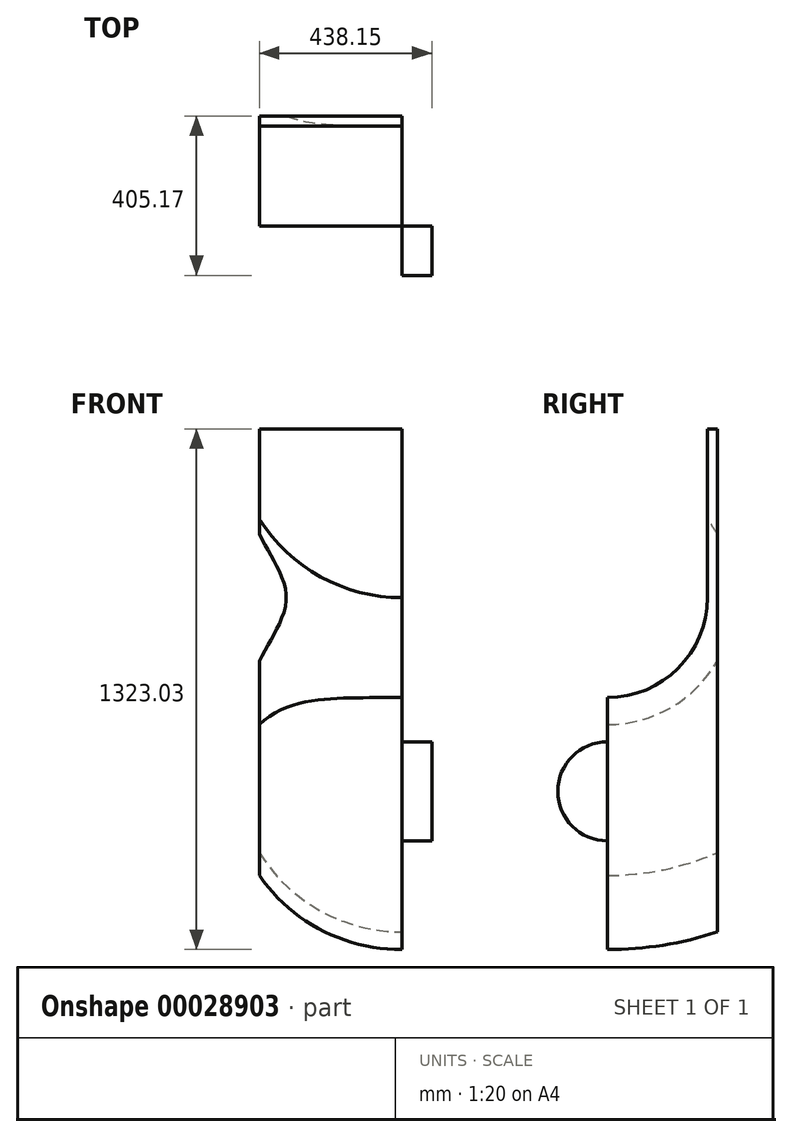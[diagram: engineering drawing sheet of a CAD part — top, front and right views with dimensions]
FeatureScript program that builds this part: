
annotation { "Feature Type Name" : "Feature", "Feature Type Description" : "" }
export const myFeature = defineFeature(function(context is Context, id is Id, definition is map)
    precondition{}
    {
        {
            var Q0;
            Q0=qCreatedBy(makeId("Front.planeOp"),FACE);
            var sketch = newSketch(context, id + "F0", { "sketchPlane" : qUnion([Q0])});
            skLineSegment(sketch, "E0", {"start": v(0, 0) * mm, "end": v(2438.4, 0) * mm});
            skLineSegment(sketch, "E1", {"start": v(2438.4, 0) * mm, "end": v(2438.4, 2438.4) * mm});
            skLineSegment(sketch, "E2", {"start": v(2438.4, 2438.4) * mm, "end": v(0, 2438.4) * mm});
            skLineSegment(sketch, "E3", {"start": v(0, 2438.4) * mm, "end": v(0, 0) * mm});
            skLineSegment(sketch, "E4", {"start": v(1219.2, 0) * mm, "end": v(1219.2, 457.2) * mm});
            skLineSegment(sketch, "E5", {"start": v(1219.2, 2438.4) * mm, "end": v(1882.77, 2438.4) * mm});
            skLineSegment(sketch, "E6", {"start": v(1219.2, 2438.4) * mm, "end": v(555.62, 2438.4) * mm});
            skLineSegment(sketch, "E7", {"start": v(555.62, 1981.2) * mm, "end": v(555.62, 1371.6) * mm});
            skLineSegment(sketch, "E8", {"start": v(1882.77, 1981.2) * mm, "end": v(1882.77, 1371.6) * mm});
            skLineSegment(sketch, "E9", {"start": v(1219.2, 0) * mm, "end": v(1219.2, 1352.55) * mm});
            skLineSegment(sketch, "E10", {"start": v(555.62, 1371.6) * mm, "end": v(1882.77, 1371.6) * mm});
            skLineSegment(sketch, "E11", {"start": v(1219.2, 1701.8) * mm, "end": v(1882.77, 1701.8) * mm});
            skLineSegment(sketch, "E12", {"start": v(2076.45, 457.2) * mm, "end": v(2076.45, 1981.2) * mm});
            skLineSegment(sketch, "E13", {"start": v(1219.2, 1701.8) * mm, "end": v(555.62, 1701.8) * mm});
            skLineSegment(sketch, "E14", {"start": v(361.95, 1981.2) * mm, "end": v(361.95, 457.2) * mm});
            skLineSegment(sketch, "E15", {"start": v(0, 0) * mm, "end": v(0, 457.2) * mm});
            skLineSegment(sketch, "E16", {"start": v(0, 457.2) * mm, "end": v(361.95, 457.2) * mm});
            skLineSegment(sketch, "E17", {"start": v(0, 2438.4) * mm, "end": v(0, 1981.2) * mm});
            skLineSegment(sketch, "E18", {"start": v(0, 1981.2) * mm, "end": v(361.95, 1981.2) * mm});
            skPoint(sketch, "E19.orphan", {"position": v(361.95, 0) * mm});
            skLineSegment(sketch, "E20.trimOffspring", {"start": v(555.62, 457.2) * mm, "end": v(1882.77, 457.2) * mm});
            skLineSegment(sketch, "E21.trimOffspring", {"start": v(2076.45, 457.2) * mm, "end": v(2438.4, 457.2) * mm});
            skPoint(sketch, "E22.orphan", {"position": v(2076.45, 0) * mm});
            skPoint(sketch, "E23.orphan", {"position": v(361.95, 2438.4) * mm});
            skPoint(sketch, "E24.orphan", {"position": v(361.95, 1701.8) * mm});
            skLineSegment(sketch, "E25.trimOffspring", {"start": v(555.62, 1981.2) * mm, "end": v(1882.77, 1981.2) * mm});
            skLineSegment(sketch, "E26.trimOffspring", {"start": v(2076.45, 1981.2) * mm, "end": v(2438.4, 1981.2) * mm});
            skPoint(sketch, "E27.orphan", {"position": v(2076.45, 1701.8) * mm});
            skLineSegment(sketch, "E28", {"start": v(555.62, 0) * mm, "end": v(549.28, 0) * mm});
            skLineSegment(sketch, "E29", {"start": v(549.28, 0) * mm, "end": v(549.28, 1352.55) * mm});
            skLineSegment(sketch, "E30", {"start": v(549.28, 0) * mm, "end": v(676.27, 0) * mm});
            skLineSegment(sketch, "E31", {"start": v(676.27, 0) * mm, "end": v(676.27, 1352.55) * mm});
            skLineSegment(sketch, "E32", {"start": v(1882.77, 0) * mm, "end": v(1889.13, 0) * mm});
            skLineSegment(sketch, "E33", {"start": v(1889.13, 0) * mm, "end": v(1762.13, 0) * mm});
            skLineSegment(sketch, "E34", {"start": v(1889.13, 0) * mm, "end": v(1889.13, 1352.55) * mm});
            skLineSegment(sketch, "E35", {"start": v(1762.13, 0) * mm, "end": v(1762.13, 1352.55) * mm});
            skLineSegment(sketch, "E36", {"start": v(412.75, 1371.6) * mm, "end": v(2025.65, 1371.6) * mm});
            skPoint(sketch, "E37.orphan", {"position": v(361.95, 1371.6) * mm});
            skLineSegment(sketch, "E38", {"start": v(412.75, 1371.6) * mm, "end": v(412.75, 1352.55) * mm});
            skLineSegment(sketch, "E39", {"start": v(412.75, 1352.55) * mm, "end": v(2025.65, 1352.55) * mm});
            skLineSegment(sketch, "E40", {"start": v(2025.65, 1352.55) * mm, "end": v(2025.65, 1371.6) * mm});
            skLineSegment(sketch, "E41.trimOffspring", {"start": v(1882.77, 1352.55) * mm, "end": v(1882.77, 0) * mm});
            skLineSegment(sketch, "E42.trimOffspring", {"start": v(1889.13, 1371.6) * mm, "end": v(1889.13, 2438.4) * mm});
            skLineSegment(sketch, "E43.trimOffspring", {"start": v(1762.13, 1371.6) * mm, "end": v(1762.13, 2438.4) * mm});
            skLineSegment(sketch, "E44.trimOffspring", {"start": v(1219.2, 1371.6) * mm, "end": v(1219.2, 1701.8) * mm});
            skLineSegment(sketch, "E45.trimOffspring", {"start": v(1219.2, 1371.6) * mm, "end": v(1219.2, 1981.2) * mm});
            skLineSegment(sketch, "E46.trimOffspring", {"start": v(549.28, 1371.6) * mm, "end": v(549.28, 2438.4) * mm});
            skLineSegment(sketch, "E47.trimOffspring", {"start": v(555.62, 1352.55) * mm, "end": v(555.62, 0) * mm});
            skLineSegment(sketch, "E48.trimOffspring", {"start": v(676.27, 1371.6) * mm, "end": v(676.27, 2438.4) * mm});
            skSolve(sketch);
        }
        {
            var Q0;
            Q0=makeQuery(id+"F0.imprint","IMPRINT",FACE,{"disambiguationData":[TD([[makeQuery(id+"F0.imprint","IMPRINT",EDGE,{"derivedFrom":sQuery(id+"F0.wireOp",EDGE,"E12")}),-1.0]])]});
            extrude(context, id + "F1", {"entities" : qUnion([Q0]), "depth" : 25.4 * mm});
        }
        {
            var Q0;
            Q0=makeQuery(id+"F1.opExtrude","CAP_FACE",FACE,{"disambiguationData":[OSD([sQuery(id+"F0.wireOp",EDGE,"E1"),sQuery(id+"F0.wireOp",EDGE,"E12"),sQuery(id+"F0.wireOp",EDGE,"E21.trimOffspring"),sQuery(id+"F0.wireOp",EDGE,"E26.trimOffspring")])],"isStart":false});
            var sketch = newSketch(context, id + "F2", { "sketchPlane" : qUnion([Q0])});
            skLineSegment(sketch, "E49.bottom", {"start": v(2076.45, 1552.47) * mm, "end": v(2438.4, 1552.47) * mm});
            skLineSegment(sketch, "E49.top", {"start": v(2076.45, 457.2) * mm, "end": v(2438.4, 457.2) * mm});
            skLineSegment(sketch, "E49.left", {"start": v(2076.45, 1552.47) * mm, "end": v(2076.45, 457.2) * mm});
            skLineSegment(sketch, "E49.right", {"start": v(2438.4, 1552.47) * mm, "end": v(2438.4, 457.2) * mm});
            skSolve(sketch);
        }
        {
            var Q0;
            Q0=makeQuery(id+"F2.imprint","IMPRINT",FACE,{"disambiguationData":[TD([[makeQuery(id+"F2.imprint","IMPRINT",EDGE,{"derivedFrom":sQuery(id+"F2.wireOp",EDGE,"E49.bottom")}),-1.0]])]});
            extrude(context, id + "F3", {"entities" : qUnion([Q0]), "operationType" : NewBodyOperationType.ADD, "depth" : 254 * mm});
        }
        {
            var Q0;
            Q0=makeQuery(id+"F1.opExtrude","CAP_FACE",FACE,{"disambiguationData":[OSD([sQuery(id+"F0.wireOp",EDGE,"E1"),sQuery(id+"F0.wireOp",EDGE,"E12"),sQuery(id+"F0.wireOp",EDGE,"E21.trimOffspring"),sQuery(id+"F0.wireOp",EDGE,"E26.trimOffspring")])],"isStart":false});
            var sketch = newSketch(context, id + "F4", { "sketchPlane" : qUnion([Q0])});
            skCircle(sketch, "E50", {"center": v(2438.4, 1981.2) * mm, "radius": 428.73 * mm});
            skSolve(sketch);
        }
        {
            var Q0;
            {var subQ3=makeQuery(id+"F1.opExtrude","CAP_EDGE",EDGE,{"disambiguationData":[OSD([sQuery(id+"F0.wireOp",EDGE,"E26.trimOffspring")])],"isStart":false});Q0=makeQuery(id+"F4.imprint","IMPRINT",FACE,{"disambiguationData":[TD([[makeQuery(id+"F4.imprint","IMPRINT",EDGE,{"derivedFrom":subQ3}),1.0]])]});}
            var Q1;
            {var subQ4=makeQuery(id+"F1.opExtrude","CAP_EDGE",EDGE,{"disambiguationData":[OSD([sQuery(id+"F0.wireOp",EDGE,"E26.trimOffspring")])],"isStart":false});Q1=makeQuery(id+"F4.imprint","IMPRINT",FACE,{"disambiguationData":[TD([[makeQuery(id+"F4.imprint","IMPRINT",EDGE,{"derivedFrom":subQ4}),-1.0]])]});}
            var Q2;
            Q2=makeQuery(id+"F3.opExtrude","CAP_EDGE",EDGE,{"disambiguationData":[OSD([sQuery(id+"F2.wireOp",EDGE,"E49.bottom")])],"isStart":false});
            revolve(context, id + "F5", {"operationType" : NewBodyOperationType.INTERSECT, "entities" : qUnion([Q0, Q1]), "axis" : qUnion([Q2]), "revolveType" : RevolveType.FULL, "oppositeDirection" : true});
        }
        {
            var Q0;
            Q0=makeQuery(id+"F3.boolean.opBoolean","MERGE",FACE,{"derivedFrom":[makeQuery(id+"F1.opExtrude","SWEPT_FACE",FACE,{"disambiguationData":[OSD([sQuery(id+"F0.wireOp",EDGE,"E1")])]}),makeQuery(id+"F3.opExtrude","SWEPT_FACE",FACE,{"disambiguationData":[OSD([sQuery(id+"F2.wireOp",EDGE,"E49.right")])]})]});
            var sketch = newSketch(context, id + "F6", { "sketchPlane" : qUnion([Q0])});
            skCircle(sketch, "E51", {"center": v(-279.4, 1060.25) * mm, "radius": 125.77 * mm});
            skSolve(sketch);
        }
        {
            var Q0;
            {var subQ0=makeQuery(id+"F3.opExtrude","CAP_EDGE",EDGE,{"disambiguationData":[OSD([sQuery(id+"F2.wireOp",EDGE,"E49.right")])],"isStart":false});var subQ1=sQuery(id+"F6.wireOp",EDGE,"E51");var subQ3=makeQuery(id+"F6.imprint","INTERSECT",VERTEX,{"disambiguationData":[OD(0.0)],"derivedFrom":[subQ0,subQ1]});Q0=makeQuery(id+"F6.imprint","IMPRINT",FACE,{"disambiguationData":[TD([[makeQuery(id+"F6.imprint","IMPRINT",EDGE,{"disambiguationData":[TD([[subQ3,1.0]])],"derivedFrom":subQ1}),1.0]])]});}
            extrude(context, id + "F7", {"entities" : qUnion([Q0]), "operationType" : NewBodyOperationType.ADD, "depth" : 76.2 * mm});
        }
    });
